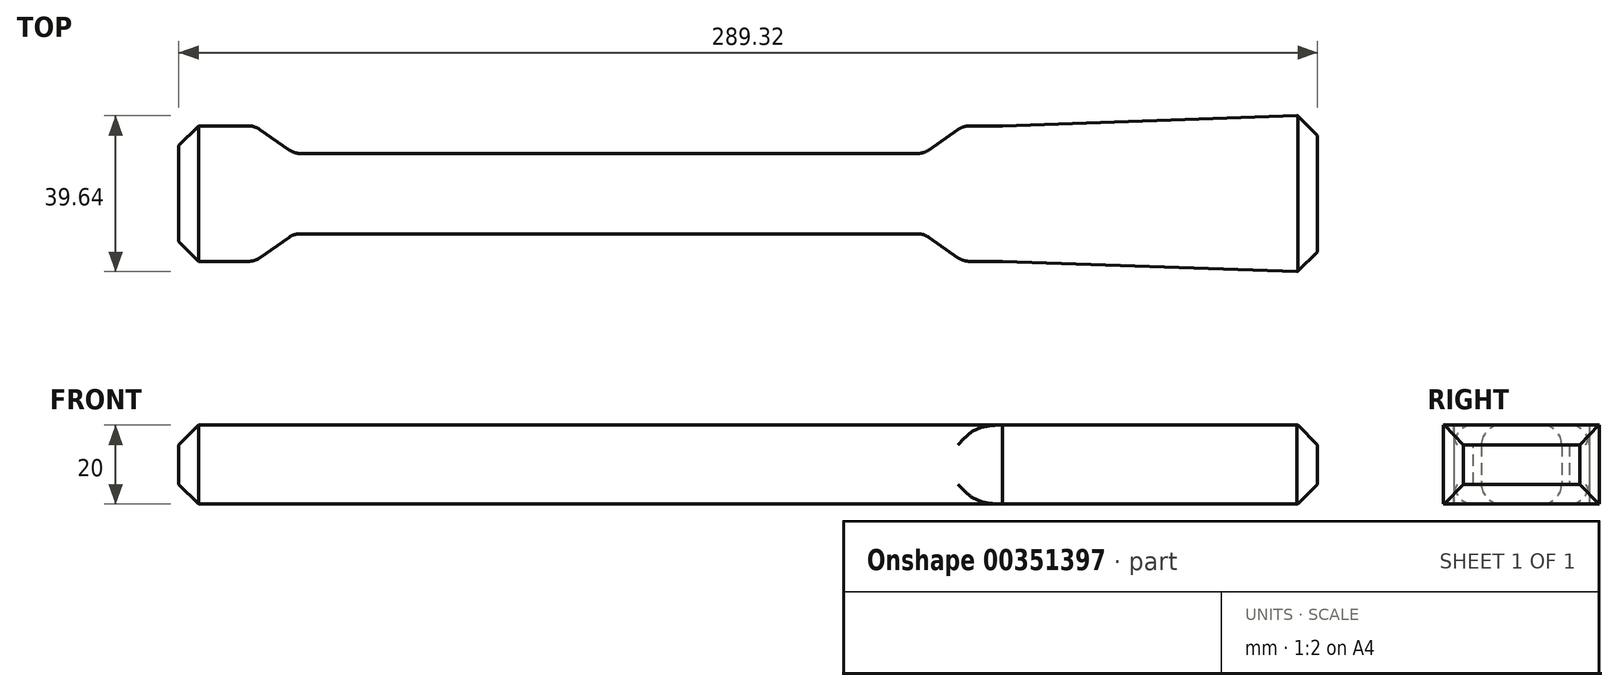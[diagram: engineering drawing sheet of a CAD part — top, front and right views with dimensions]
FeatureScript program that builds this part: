
annotation { "Feature Type Name" : "Feature", "Feature Type Description" : "" }
export const myFeature = defineFeature(function(context is Context, id is Id, definition is map)
    precondition{}
    {
        {
            var Q0;
            Q0=qCreatedBy(makeId("Top.planeOp"),FACE);
            var sketch = newSketch(context, id + "F0", { "sketchPlane" : qUnion([Q0])});
            skLineSegment(sketch, "E0.bottom", {"start": v(25.74, 19.2) * mm, "end": v(-54.26, 22) * mm});
            skLineSegment(sketch, "E0.top", {"start": v(25.74, 59.2) * mm, "end": v(-54.26, 56.4) * mm});
            skLineSegment(sketch, "E0.left", {"start": v(25.74, 19.2) * mm, "end": v(25.74, 59.2) * mm});
            skLineSegment(sketch, "E0.right", {"start": v(-54.26, 22) * mm, "end": v(-54.26, 56.4) * mm});
            skPoint(sketch, "E0.middle", {"position": v(-14.26, 37.8) * mm});
            skLineSegment(sketch, "E1", {"start": v(-54.26, 56.4) * mm, "end": v(-64.26, 56.4) * mm});
            skLineSegment(sketch, "E2", {"start": v(-64.26, 56.4) * mm, "end": v(-64.26, 22) * mm});
            skLineSegment(sketch, "E3", {"start": v(-64.26, 22) * mm, "end": v(-54.26, 22) * mm});
            skLineSegment(sketch, "E4", {"start": v(-64.26, 56.4) * mm, "end": v(-72.97, 50.31) * mm});
            skLineSegment(sketch, "E5", {"start": v(-75.84, 49.4) * mm, "end": v(-232.68, 49.4) * mm});
            skLineSegment(sketch, "E6", {"start": v(-235.55, 50.31) * mm, "end": v(-242.97, 55.5) * mm});
            skLineSegment(sketch, "E7", {"start": v(-245.84, 56.4) * mm, "end": v(-263.58, 56.4) * mm});
            skPoint(sketch, "E8.visualSharp", {"position": v(-74.26, 49.4) * mm});
            skArc(sketch, "E8.filletArc", {"start": v(-75.84, 49.4) * mm, "mid": v(-74.33, 49.64) * mm, "end": v(-72.97, 50.31) * mm});
            skPoint(sketch, "E9.visualSharp", {"position": v(-64.26, 56.4) * mm});
            skPoint(sketch, "E10.visualSharp", {"position": v(-234.26, 49.4) * mm});
            skArc(sketch, "E10.filletArc", {"start": v(-235.55, 50.31) * mm, "mid": v(-234.19, 49.64) * mm, "end": v(-232.68, 49.4) * mm});
            skPoint(sketch, "E11.visualSharp", {"position": v(-244.26, 56.4) * mm});
            skArc(sketch, "E11.filletArc", {"start": v(-242.97, 55.5) * mm, "mid": v(-244.33, 56.18) * mm, "end": v(-245.84, 56.4) * mm});
            skLineSegment(sketch, "E12.MirrorCS", {"start": v(-245.84, 22) * mm, "end": v(-263.58, 22) * mm});
            skArc(sketch, "E13.MirrorCS", {"start": v(-242.97, 22.9) * mm, "mid": v(-244.33, 22.23) * mm, "end": v(-245.84, 22) * mm});
            skLineSegment(sketch, "E14.MirrorCS", {"start": v(-235.55, 28.1) * mm, "end": v(-242.97, 22.9) * mm});
            skArc(sketch, "E15.MirrorCS", {"start": v(-235.55, 28.1) * mm, "mid": v(-234.19, 28.77) * mm, "end": v(-232.68, 29) * mm});
            skLineSegment(sketch, "E16.MirrorCS", {"start": v(-64.26, 22) * mm, "end": v(-72.97, 28.1) * mm});
            skLineSegment(sketch, "E17.MirrorCS", {"start": v(-75.84, 29) * mm, "end": v(-232.68, 29) * mm});
            skArc(sketch, "E18.MirrorCS", {"start": v(-75.84, 29) * mm, "mid": v(-74.33, 28.77) * mm, "end": v(-72.97, 28.1) * mm});
            skLineSegment(sketch, "E19", {"start": v(-263.58, 56.4) * mm, "end": v(-263.58, 22) * mm});
            skSolve(sketch);
        }
        {
            var Q0;
            Q0=makeQuery(id+"F0.imprint","IMPRINT",FACE,{"disambiguationData":[TD([[makeQuery(id+"F0.imprint","IMPRINT",EDGE,{"derivedFrom":sQuery(id+"F0.wireOp",EDGE,"E0.bottom")}),-1.0]])]});
            var Q1;
            Q1=makeQuery(id+"F0.imprint","IMPRINT",FACE,{"disambiguationData":[TD([[makeQuery(id+"F0.imprint","IMPRINT",EDGE,{"derivedFrom":sQuery(id+"F0.wireOp",EDGE,"E0.right")}),1.0]])]});
            var Q2;
            Q2=makeQuery(id+"F0.imprint","IMPRINT",FACE,{"disambiguationData":[TD([[makeQuery(id+"F0.imprint","IMPRINT",EDGE,{"derivedFrom":sQuery(id+"F0.wireOp",EDGE,"E2")}),-1.0]])]});
            extrude(context, id + "F1", {"entities" : qUnion([Q0, Q1, Q2]), "depth" : 20 * mm});
        }
        {
            var Q0;
            Q0=makeQuery(id+"F1.opExtrude","SWEPT_EDGE",EDGE,{"disambiguationData":[OSD([sQuery(id+"F0.wireOp",EDGE,"E2"),sQuery(id+"F0.wireOp",EDGE,"E3"),sQuery(id+"F0.wireOp",EDGE,"E16.MirrorCS")])]});
            var Q1;
            Q1=makeQuery(id+"F1.opExtrude","SWEPT_EDGE",EDGE,{"disambiguationData":[OSD([sQuery(id+"F0.wireOp",EDGE,"E1"),sQuery(id+"F0.wireOp",EDGE,"E2"),sQuery(id+"F0.wireOp",EDGE,"E4")])]});
            var Q2;
            Q2=makeQuery(id+"F1.opExtrude","CAP_EDGE",EDGE,{"disambiguationData":[OSD([sQuery(id+"F0.wireOp",EDGE,"E5")])],"isStart":true});
            var Q3;
            Q3=makeQuery(id+"F1.opExtrude","CAP_EDGE",EDGE,{"disambiguationData":[OSD([sQuery(id+"F0.wireOp",EDGE,"E17.MirrorCS")])],"isStart":true});
            var Q4;
            Q4=makeQuery(id+"F1.opExtrude","CAP_EDGE",EDGE,{"disambiguationData":[OSD([sQuery(id+"F0.wireOp",EDGE,"E7")])],"isStart":true});
            var Q5;
            Q5=makeQuery(id+"F1.opExtrude","CAP_EDGE",EDGE,{"disambiguationData":[OSD([sQuery(id+"F0.wireOp",EDGE,"E12.MirrorCS")])],"isStart":true});
            var Q6;
            Q6=makeQuery(id+"F1.opExtrude","CAP_EDGE",EDGE,{"disambiguationData":[OSD([sQuery(id+"F0.wireOp",EDGE,"E10.filletArc")])],"isStart":true});
            var Q7;
            Q7=makeQuery(id+"F1.opExtrude","CAP_EDGE",EDGE,{"disambiguationData":[OSD([sQuery(id+"F0.wireOp",EDGE,"E6")])],"isStart":true});
            var Q8;
            Q8=makeQuery(id+"F1.opExtrude","CAP_EDGE",EDGE,{"disambiguationData":[OSD([sQuery(id+"F0.wireOp",EDGE,"E11.filletArc")])],"isStart":true});
            var Q9;
            Q9=makeQuery(id+"F1.opExtrude","CAP_EDGE",EDGE,{"disambiguationData":[OSD([sQuery(id+"F0.wireOp",EDGE,"E13.MirrorCS")])],"isStart":true});
            var Q10;
            Q10=makeQuery(id+"F1.opExtrude","CAP_EDGE",EDGE,{"disambiguationData":[OSD([sQuery(id+"F0.wireOp",EDGE,"E14.MirrorCS")])],"isStart":true});
            var Q11;
            Q11=makeQuery(id+"F1.opExtrude","CAP_EDGE",EDGE,{"disambiguationData":[OSD([sQuery(id+"F0.wireOp",EDGE,"E15.MirrorCS")])],"isStart":true});
            var Q12;
            Q12=makeQuery(id+"F1.opExtrude","CAP_EDGE",EDGE,{"disambiguationData":[OSD([sQuery(id+"F0.wireOp",EDGE,"E7")])],"isStart":false});
            var Q13;
            Q13=makeQuery(id+"F1.opExtrude","CAP_EDGE",EDGE,{"disambiguationData":[OSD([sQuery(id+"F0.wireOp",EDGE,"E11.filletArc")])],"isStart":false});
            var Q14;
            Q14=makeQuery(id+"F1.opExtrude","CAP_EDGE",EDGE,{"disambiguationData":[OSD([sQuery(id+"F0.wireOp",EDGE,"E6")])],"isStart":false});
            var Q15;
            Q15=makeQuery(id+"F1.opExtrude","CAP_EDGE",EDGE,{"disambiguationData":[OSD([sQuery(id+"F0.wireOp",EDGE,"E10.filletArc")])],"isStart":false});
            var Q16;
            Q16=makeQuery(id+"F1.opExtrude","CAP_EDGE",EDGE,{"disambiguationData":[OSD([sQuery(id+"F0.wireOp",EDGE,"E5")])],"isStart":false});
            var Q17;
            Q17=makeQuery(id+"F1.opExtrude","CAP_EDGE",EDGE,{"disambiguationData":[OSD([sQuery(id+"F0.wireOp",EDGE,"E12.MirrorCS")])],"isStart":false});
            var Q18;
            Q18=makeQuery(id+"F1.opExtrude","CAP_EDGE",EDGE,{"disambiguationData":[OSD([sQuery(id+"F0.wireOp",EDGE,"E13.MirrorCS")])],"isStart":false});
            var Q19;
            Q19=makeQuery(id+"F1.opExtrude","CAP_EDGE",EDGE,{"disambiguationData":[OSD([sQuery(id+"F0.wireOp",EDGE,"E14.MirrorCS")])],"isStart":false});
            var Q20;
            Q20=makeQuery(id+"F1.opExtrude","CAP_EDGE",EDGE,{"disambiguationData":[OSD([sQuery(id+"F0.wireOp",EDGE,"E15.MirrorCS")])],"isStart":false});
            var Q21;
            Q21=makeQuery(id+"F1.opExtrude","CAP_EDGE",EDGE,{"disambiguationData":[OSD([sQuery(id+"F0.wireOp",EDGE,"E17.MirrorCS")])],"isStart":false});
            var Q22;
            Q22=makeQuery(id+"F1.opExtrude","CAP_EDGE",EDGE,{"disambiguationData":[OSD([sQuery(id+"F0.wireOp",EDGE,"E18.MirrorCS")])],"isStart":false});
            var Q23;
            Q23=makeQuery(id+"F1.opExtrude","CAP_EDGE",EDGE,{"disambiguationData":[OSD([sQuery(id+"F0.wireOp",EDGE,"E16.MirrorCS")])],"isStart":false});
            var Q24;
            Q24=makeQuery(id+"F1.opExtrude","CAP_EDGE",EDGE,{"disambiguationData":[OSD([sQuery(id+"F0.wireOp",EDGE,"E16.MirrorCS")])],"isStart":true});
            var Q25;
            Q25=makeQuery(id+"F1.opExtrude","CAP_EDGE",EDGE,{"disambiguationData":[OSD([sQuery(id+"F0.wireOp",EDGE,"E18.MirrorCS")])],"isStart":true});
            var Q26;
            Q26=makeQuery(id+"F1.opExtrude","CAP_EDGE",EDGE,{"disambiguationData":[OSD([sQuery(id+"F0.wireOp",EDGE,"E8.filletArc")])],"isStart":false});
            var Q27;
            Q27=makeQuery(id+"F1.opExtrude","CAP_EDGE",EDGE,{"disambiguationData":[OSD([sQuery(id+"F0.wireOp",EDGE,"E8.filletArc")])],"isStart":true});
            var Q28;
            Q28=makeQuery(id+"F1.opExtrude","CAP_EDGE",EDGE,{"disambiguationData":[OSD([sQuery(id+"F0.wireOp",EDGE,"E4")])],"isStart":true});
            var Q29;
            Q29=makeQuery(id+"F1.opExtrude","CAP_EDGE",EDGE,{"disambiguationData":[OSD([sQuery(id+"F0.wireOp",EDGE,"E4")])],"isStart":false});
            fillet(context, id + "F2", {"entities" : qUnion([Q0, Q1, Q2, Q3, Q4, Q5, Q6, Q7, Q8, Q9, Q10, Q11, Q12, Q13, Q14, Q15, Q16, Q17, Q18, Q19, Q20, Q21, Q22, Q23, Q24, Q25, Q26, Q27, Q28, Q29]), "radius" : 5 * mm, "tangentPropagation" : true, "allowEdgeOverflow" : false});
        }
        {
            var Q0;
            Q0=makeQuery(id+"F1.opExtrude","SWEPT_FACE",FACE,{"disambiguationData":[OSD([sQuery(id+"F0.wireOp",EDGE,"E19")])]});
            chamfer(context, id + "F3", {"entities" : qUnion([Q0]), "width" : 5 * mm, "tangentPropagation" : true});
        }
        {
            var Q0;
            Q0=makeQuery(id+"F1.opExtrude","SWEPT_FACE",FACE,{"disambiguationData":[OSD([sQuery(id+"F0.wireOp",EDGE,"E0.left")])]});
            chamfer(context, id + "F4", {"entities" : qUnion([Q0]), "width" : 5 * mm, "tangentPropagation" : true});
        }
    });
